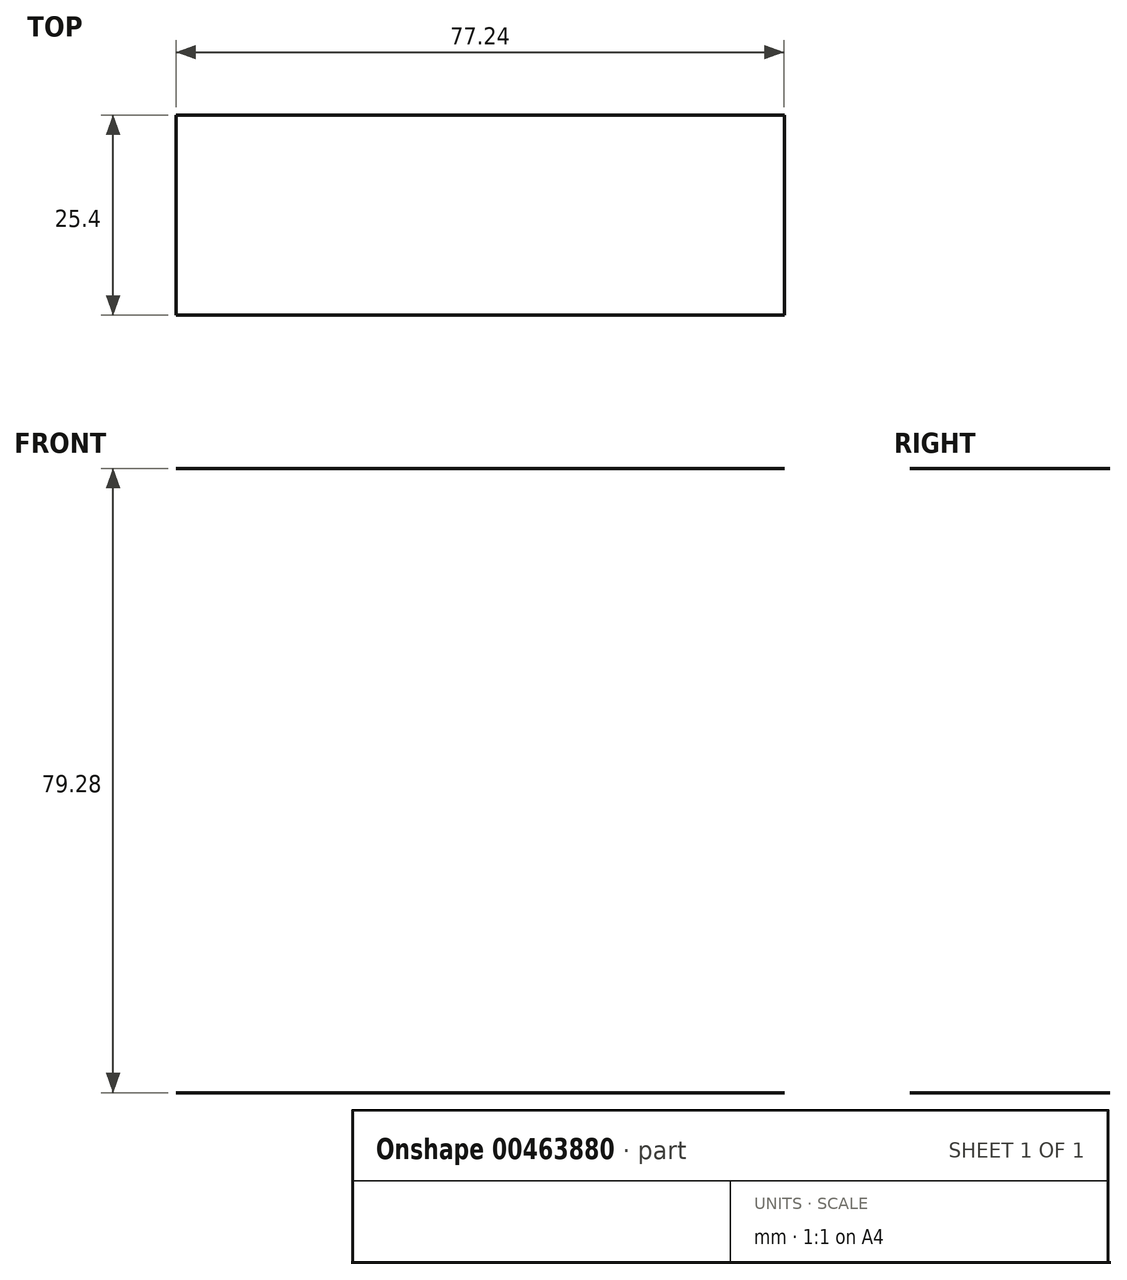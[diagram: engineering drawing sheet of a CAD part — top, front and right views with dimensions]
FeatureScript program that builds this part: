
annotation { "Feature Type Name" : "Feature", "Feature Type Description" : "" }
export const myFeature = defineFeature(function(context is Context, id is Id, definition is map)
    precondition{}
    {
        {
            var Q0;
            Q0=qCreatedBy(makeId("Front.planeOp"),FACE);
            var sketch = newSketch(context, id + "F0", { "sketchPlane" : qUnion([Q0])});
            skLineSegment(sketch, "E0.bottom", {"start": v(-25.75, 34.22) * mm, "end": v(51.5, 34.22) * mm});
            skLineSegment(sketch, "E0.top", {"start": v(-25.75, -45.06) * mm, "end": v(51.5, -45.06) * mm});
            skLineSegment(sketch, "E0.left", {"start": v(-25.75, 34.22) * mm, "end": v(-25.75, -45.06) * mm});
            skLineSegment(sketch, "E0.right", {"start": v(51.5, 34.22) * mm, "end": v(51.5, -45.06) * mm});
            skSolve(sketch);
        }
        {
            var Q0;
            Q0=sQuery(id+"F0.wireOp",EDGE,"E0.bottom");
            var Q1;
            Q1=sQuery(id+"F0.wireOp",EDGE,"E0.top");
            extrude(context, id + "F1", {"bodyType" : ToolBodyType.SURFACE, "surfaceEntities" : qUnion([Q0, Q1]), "depth" : 25.4 * mm});
        }
    });
